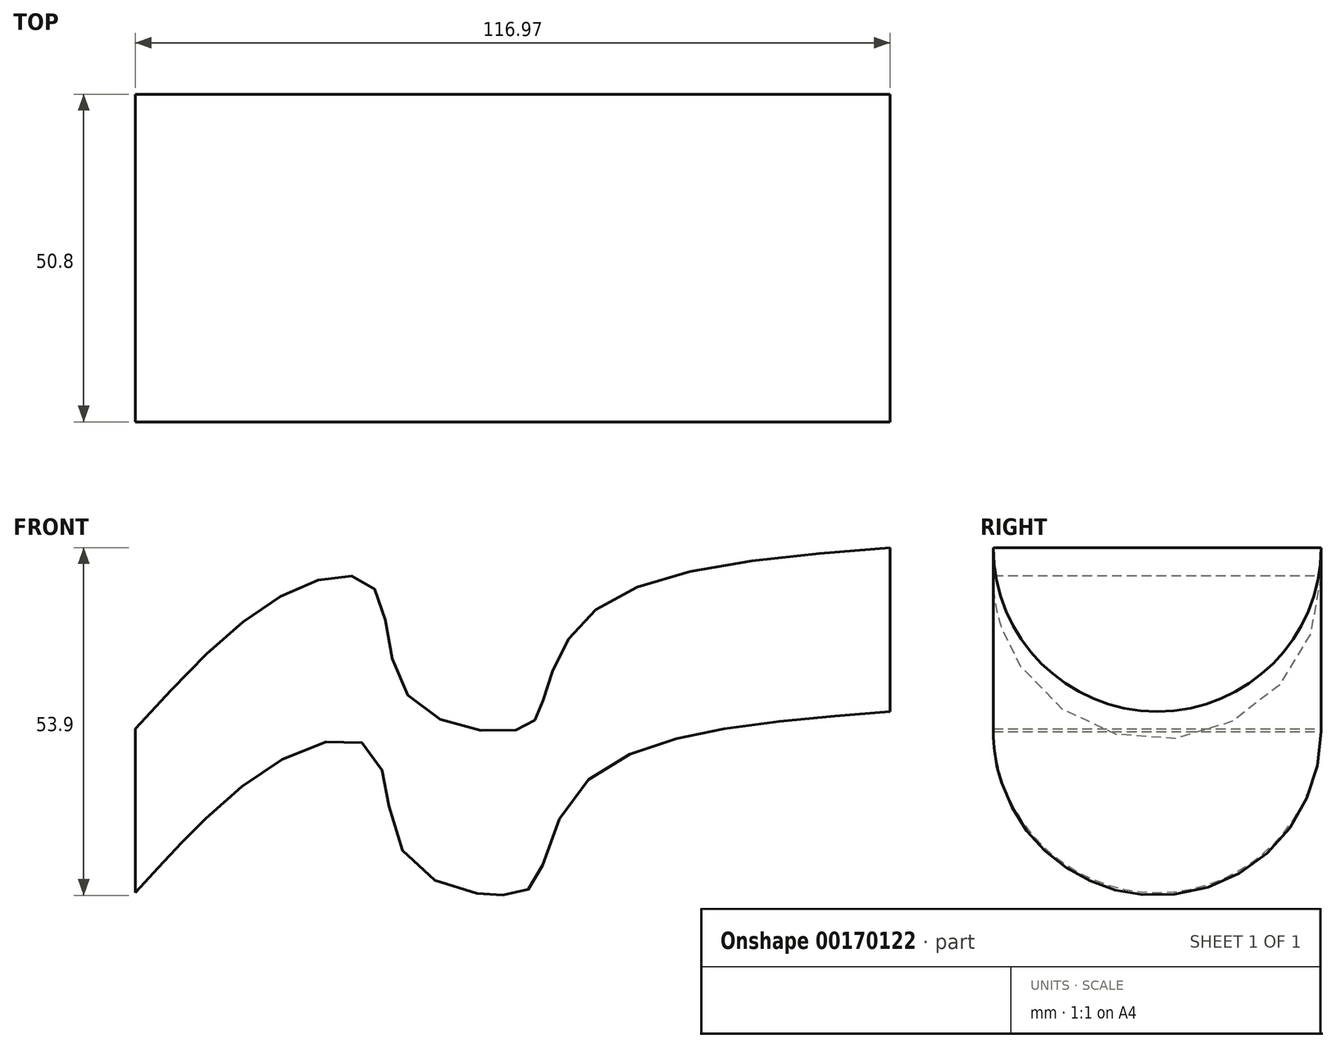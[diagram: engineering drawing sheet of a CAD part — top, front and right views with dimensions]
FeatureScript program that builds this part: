
annotation { "Feature Type Name" : "Feature", "Feature Type Description" : "" }
export const myFeature = defineFeature(function(context is Context, id is Id, definition is map)
    precondition{}
    {
        {
            var Q0;
            Q0=qCreatedBy(makeId("Right.planeOp"),FACE);
            var sketch = newSketch(context, id + "F0", { "sketchPlane" : qUnion([Q0])});
            skArc(sketch, "E0", {"start": v(0, 0) * mm, "mid": v(25.4, -25.4) * mm, "end": v(50.8, 0) * mm});
            skLineSegment(sketch, "E1", {"start": v(0, 0) * mm, "end": v(50.8, 0) * mm});
            skSolve(sketch);
        }
        {
            var Q0;
            Q0=qCreatedBy(makeId("Front.planeOp"),FACE);
            cPlane(context, id + "F1", {"entities" : qUnion([Q0]), "cplaneType" : CPlaneType.OFFSET, "offset" : 25.4 * mm, "oppositeDirection" : true, "width" : 152.4 * mm, "height" : 152.4 * mm});
        }
        {
            var Q0;
            Q0=qCreatedBy(id+"F1.planeOp",FACE);
            var sketch = newSketch(context, id + "F2", { "sketchPlane" : qUnion([Q0])});
            skFitSpline(sketch, "E2", {"points": [v(0, 0) * mm, v(23.54, 21.1) * mm, v(36.85, 21.96) * mm, v(42.45, 4.96) * mm, v(59.87, 0) * mm, v(63.05, 4.05) * mm, v(70.77, 17.99) * mm, v(116.97, 28.07) * mm], "startDerivative": vector(126.53, 138.72) * mm, "endDerivative": vector(253.18, 19.63) * mm});
            skSolve(sketch);
        }
        {
            var Q0;
            Q0=makeQuery(id+"F0.imprint","IMPRINT",FACE,{"disambiguationData":[TD([[makeQuery(id+"F0.imprint","IMPRINT",EDGE,{"derivedFrom":sQuery(id+"F0.wireOp",EDGE,"E0")}),1.0]])]});
            var Q1;
            Q1=sQuery(id+"F2.wireOp",EDGE,"E2");
            sweep(context, id + "F3", {"profiles" : qUnion([Q0]), "path" : qUnion([Q1]), "keepProfileOrientation" : true});
        }
    });
